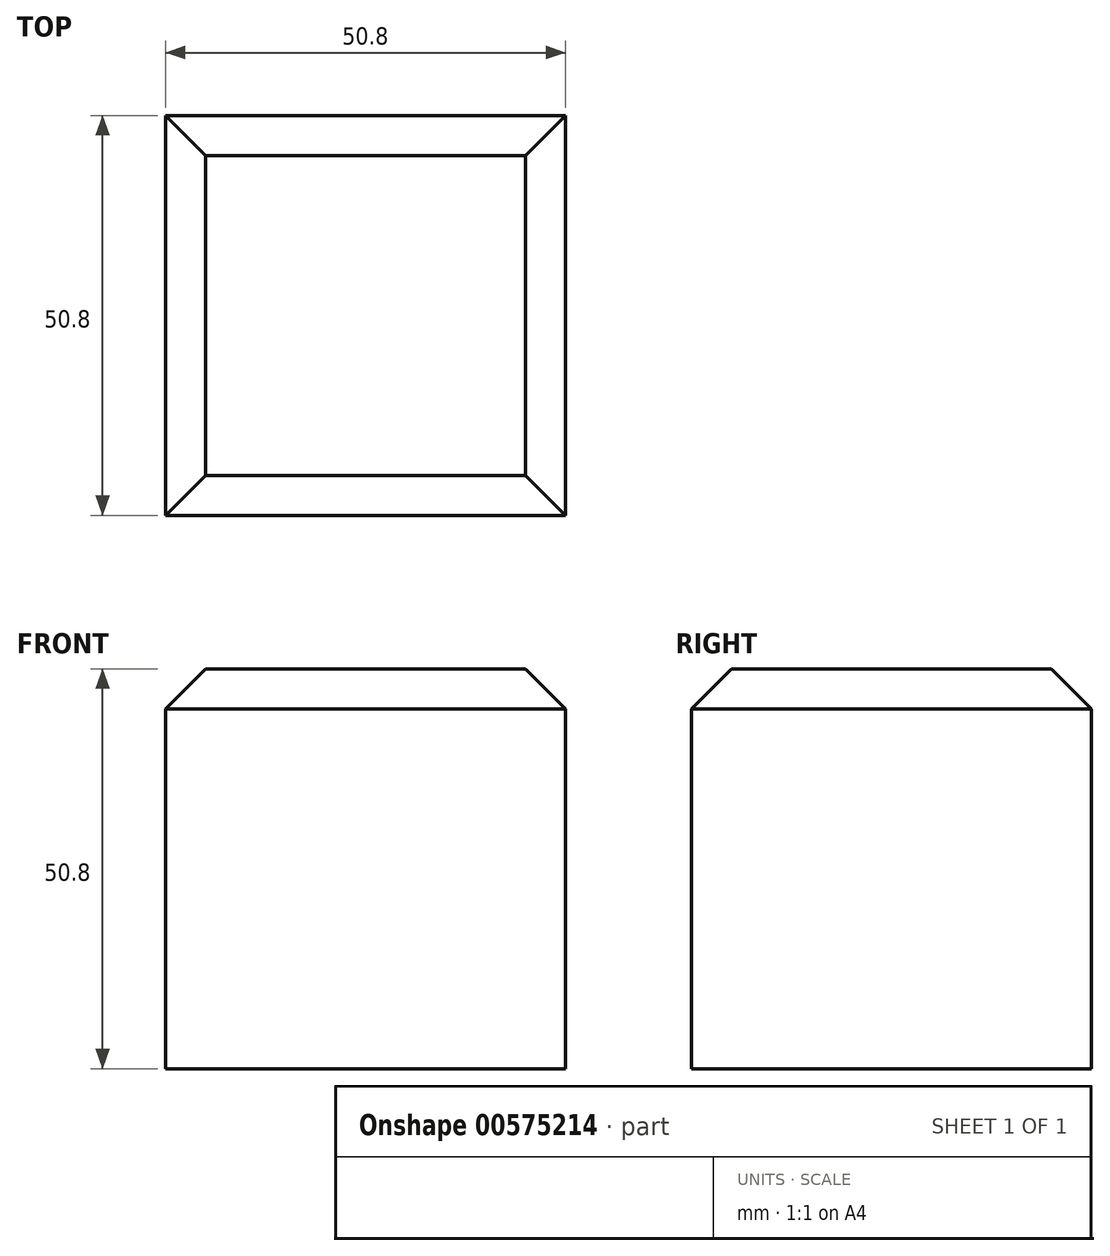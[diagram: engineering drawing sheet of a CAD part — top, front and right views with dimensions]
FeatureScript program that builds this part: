
annotation { "Feature Type Name" : "Feature", "Feature Type Description" : "" }
export const myFeature = defineFeature(function(context is Context, id is Id, definition is map)
    precondition{}
    {
        {
            var Q0;
            Q0=qCreatedBy(makeId("Front.planeOp"),FACE);
            var sketch = newSketch(context, id + "F0", { "sketchPlane" : qUnion([Q0])});
            skLineSegment(sketch, "E0.bottom", {"start": v(24.68, 25.4) * mm, "end": v(-26.12, 25.4) * mm});
            skLineSegment(sketch, "E0.top", {"start": v(24.68, -25.4) * mm, "end": v(-26.12, -25.4) * mm});
            skLineSegment(sketch, "E0.left", {"start": v(24.68, 25.4) * mm, "end": v(24.68, -25.4) * mm});
            skLineSegment(sketch, "E0.right", {"start": v(-26.12, 25.4) * mm, "end": v(-26.12, -25.4) * mm});
            skPoint(sketch, "E0.middle", {"position": v(-0.72, 0) * mm});
            skSolve(sketch);
        }
        {
            var Q0;
            Q0 = qSketchRegion(id + "F0", true);
            extrude(context, id + "F1", {"entities" : qUnion([Q0]), "depth" : 50.8 * mm, "offsetDistance" : 25.4 * mm});
        }
        {
            var Q0;
            Q0=makeQuery(id+"F1.opExtrude","SWEPT_FACE",FACE,{"disambiguationData":[OSD([sQuery(id+"F0.wireOp",EDGE,"E0.bottom")])]});
            chamfer(context, id + "F2", {"entities" : qUnion([Q0]), "width" : 5.08 * mm, "tangentPropagation" : true});
        }
    });
